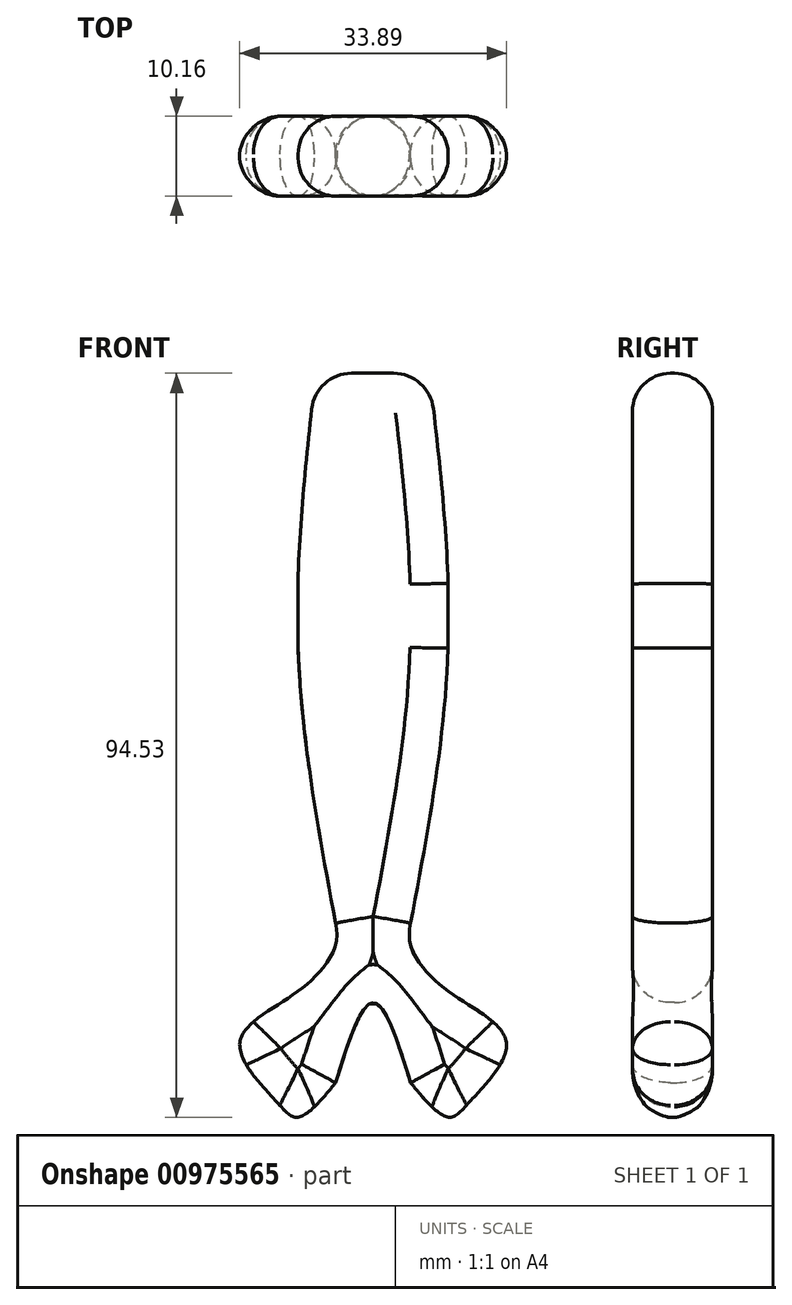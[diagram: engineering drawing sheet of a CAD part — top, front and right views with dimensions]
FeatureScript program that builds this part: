
annotation { "Feature Type Name" : "Feature", "Feature Type Description" : "" }
export const myFeature = defineFeature(function(context is Context, id is Id, definition is map)
    precondition{}
    {
        {
            var Q0;
            Q0=qCreatedBy(makeId("Front.planeOp"),FACE);
            var sketch = newSketch(context, id + "F0", { "sketchPlane" : qUnion([Q0])});
            skLineSegment(sketch, "E0.left", {"start": v(0, -25.77) * mm, "end": v(0, -34.93) * mm});
            skLineSegment(sketch, "E0.right", {"start": v(19.05, -26.7) * mm, "end": v(19.05, -34.93) * mm});
            skLineSegment(sketch, "E1", {"start": v(9.53, 0) * mm, "end": v(12.13, 0) * mm});
            skPoint(sketch, "E2.endSnap0", {"position": v(4.76, 0) * mm});
            skLineSegment(sketch, "E3", {"start": v(6.77, 0) * mm, "end": v(9.53, 0) * mm});
            skFitSpline(sketch, "E4", {"points": [v(2.23, 0) * mm, v(0, -34.93) * mm, v(4.76, -69.85) * mm], "startDerivative": vector(-7.96, -70.04) * mm, "endDerivative": vector(13, -69.66) * mm});
            skFitSpline(sketch, "E5", {"points": [v(16.64, 0) * mm, v(19.05, -34.93) * mm, v(14.29, -69.85) * mm], "startDerivative": vector(8.4, -70.03) * mm, "endDerivative": vector(-13.1, -69.67) * mm});
            skFitSpline(sketch, "E6", {"points": [v(4.76, -69.85) * mm, v(4.76, -72.67) * mm, v(0, -78.5) * mm, v(-7.4, -85) * mm, v(-2.83, -92.45) * mm, v(0, -94.51) * mm, v(4.76, -90.13) * mm], "startDerivative": vector(4.01, -23.53) * mm, "endDerivative": vector(30.59, 36.97) * mm});
            skFitSpline(sketch, "E7.MirrorCS", {"points": [v(14.29, -69.85) * mm, v(14.29, -72.67) * mm, v(19.05, -78.5) * mm, v(26.45, -85) * mm, v(21.88, -92.45) * mm, v(19.05, -94.51) * mm, v(14.29, -90.13) * mm], "startDerivative": vector(-4.01, -23.53) * mm, "endDerivative": vector(-30.59, 36.97) * mm});
            skPoint(sketch, "E8.orphan", {"position": v(0, -69.85) * mm});
            skPoint(sketch, "E9.end.orphan", {"position": v(9.53, -69.85) * mm});
            skPoint(sketch, "E10.orphan", {"position": v(19.05, -69.85) * mm});
            skPoint(sketch, "E11.end.orphan", {"position": v(19.05, 0) * mm});
            skPoint(sketch, "E12.start.orphan", {"position": v(14.29, 0) * mm});
            skPoint(sketch, "E0.bottom.start.orphan", {"position": v(0, 0) * mm});
            skArc(sketch, "E13.filletArc", {"start": v(6.77, 0) * mm, "mid": v(3.38, -1.3) * mm, "end": v(1.72, -4.52) * mm});
            skArc(sketch, "E14.filletArc", {"start": v(17.18, -4.49) * mm, "mid": v(15.5, -1.28) * mm, "end": v(12.13, 0) * mm});
            skFitSpline(sketch, "E15", {"points": [v(4.76, -90.13) * mm, v(9.53, -79.95) * mm, v(14.29, -90.13) * mm], "startDerivative": vector(9.53, 30.54) * mm, "endDerivative": vector(9.52, -30.54) * mm});
            skSolve(sketch);
        }
        {
            var Q0;
            Q0=makeQuery(id+"F0.imprint","IMPRINT",FACE,{"disambiguationData":[TD([[makeQuery(id+"F0.imprint","IMPRINT",EDGE,{"derivedFrom":sQuery(id+"F0.wireOp",EDGE,"E0.left")}),1.0]])]});
            var sketch = newSketch(context, id + "F1", { "sketchPlane" : qUnion([Q0])});
            skSolve(sketch);
        }
        {
            var Q0;
            Q0=makeQuery(id+"F1.imprint","IMPRINT",FACE,{"disambiguationData":[TD([[makeQuery(id+"F1.imprint","IMPRINT",EDGE,{"derivedFrom":makeQuery(id+"F0.imprint","IMPRINT",EDGE,{"derivedFrom":sQuery(id+"F0.wireOp",EDGE,"E0.left")})}),1.0]])]});
            extrude(context, id + "F2", {"entities" : qUnion([Q0]), "depth" : 10.16 * mm, "offsetDistance" : 25.4 * mm});
        }
        {
            var Q0;
            Q0=makeQuery(id+"F2.opExtrude","CAP_FACE",FACE,{"disambiguationData":[OSD([sQuery(id+"F0.wireOp",EDGE,"E0.left"),sQuery(id+"F0.wireOp",EDGE,"E0.right"),sQuery(id+"F0.wireOp",EDGE,"E1"),sQuery(id+"F0.wireOp",EDGE,"E3"),sQuery(id+"F0.wireOp",EDGE,"E4"),sQuery(id+"F0.wireOp",EDGE,"E5"),sQuery(id+"F0.wireOp",EDGE,"E6"),sQuery(id+"F0.wireOp",EDGE,"E7.MirrorCS"),sQuery(id+"F0.wireOp",EDGE,"E4"),sQuery(id+"F0.wireOp",EDGE,"E5"),sQuery(id+"F0.wireOp",EDGE,"E13.filletArc"),sQuery(id+"F0.wireOp",EDGE,"E14.filletArc"),sQuery(id+"F0.wireOp",EDGE,"E15")])],"isStart":true});
            fillet(context, id + "F3", {"entities" : qUnion([Q0]), "radius" : 4.83 * mm, "tangentPropagation" : true, "allowEdgeOverflow" : false});
        }
        {
            var Q0;
            Q0=makeQuery(id+"F2.opExtrude","SWEPT_FACE",FACE,{"disambiguationData":[OSD([sQuery(id+"F0.wireOp",EDGE,"E0.left")])]});
            var Q1;
            Q1=makeQuery(id+"F2.opExtrude","CAP_FACE",FACE,{"disambiguationData":[OSD([sQuery(id+"F0.wireOp",EDGE,"E0.left"),sQuery(id+"F0.wireOp",EDGE,"E0.right"),sQuery(id+"F0.wireOp",EDGE,"E1"),sQuery(id+"F0.wireOp",EDGE,"E3"),sQuery(id+"F0.wireOp",EDGE,"E4"),sQuery(id+"F0.wireOp",EDGE,"E5"),sQuery(id+"F0.wireOp",EDGE,"E6"),sQuery(id+"F0.wireOp",EDGE,"E7.MirrorCS"),sQuery(id+"F0.wireOp",EDGE,"E4"),sQuery(id+"F0.wireOp",EDGE,"E5"),sQuery(id+"F0.wireOp",EDGE,"E13.filletArc"),sQuery(id+"F0.wireOp",EDGE,"E14.filletArc"),sQuery(id+"F0.wireOp",EDGE,"E15")])],"isStart":false});
            fillet(context, id + "F4", {"entities" : qUnion([Q0, Q1]), "radius" : 4.83 * mm, "tangentPropagation" : true, "allowEdgeOverflow" : false});
        }
    });
